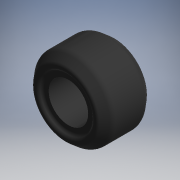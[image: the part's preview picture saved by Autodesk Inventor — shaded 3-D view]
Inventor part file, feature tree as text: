
AUTODESK INVENTOR PART (.ipt)
format: ipt  version: 2016 (Build 200138000, 138)  size: 144,384 bytes
history: native  units: mm (DEFAULTED — no unit token found)
features: fillet x1
ambient origin geometry x8: Origin, YZ Plane, XZ Plane, XY Plane, X Axis, Y Axis, Z Axis, Center Point
bodies: Solid1 (feature_tree)
feature tree (1):
  fillet  "Fillet3"  [1 undecoded]
note: 1 required parameter value undecoded (feature->parameter linkage not recoverable at this tier; creation-order binding heuristic only, values carry confidence <= 0.55)
